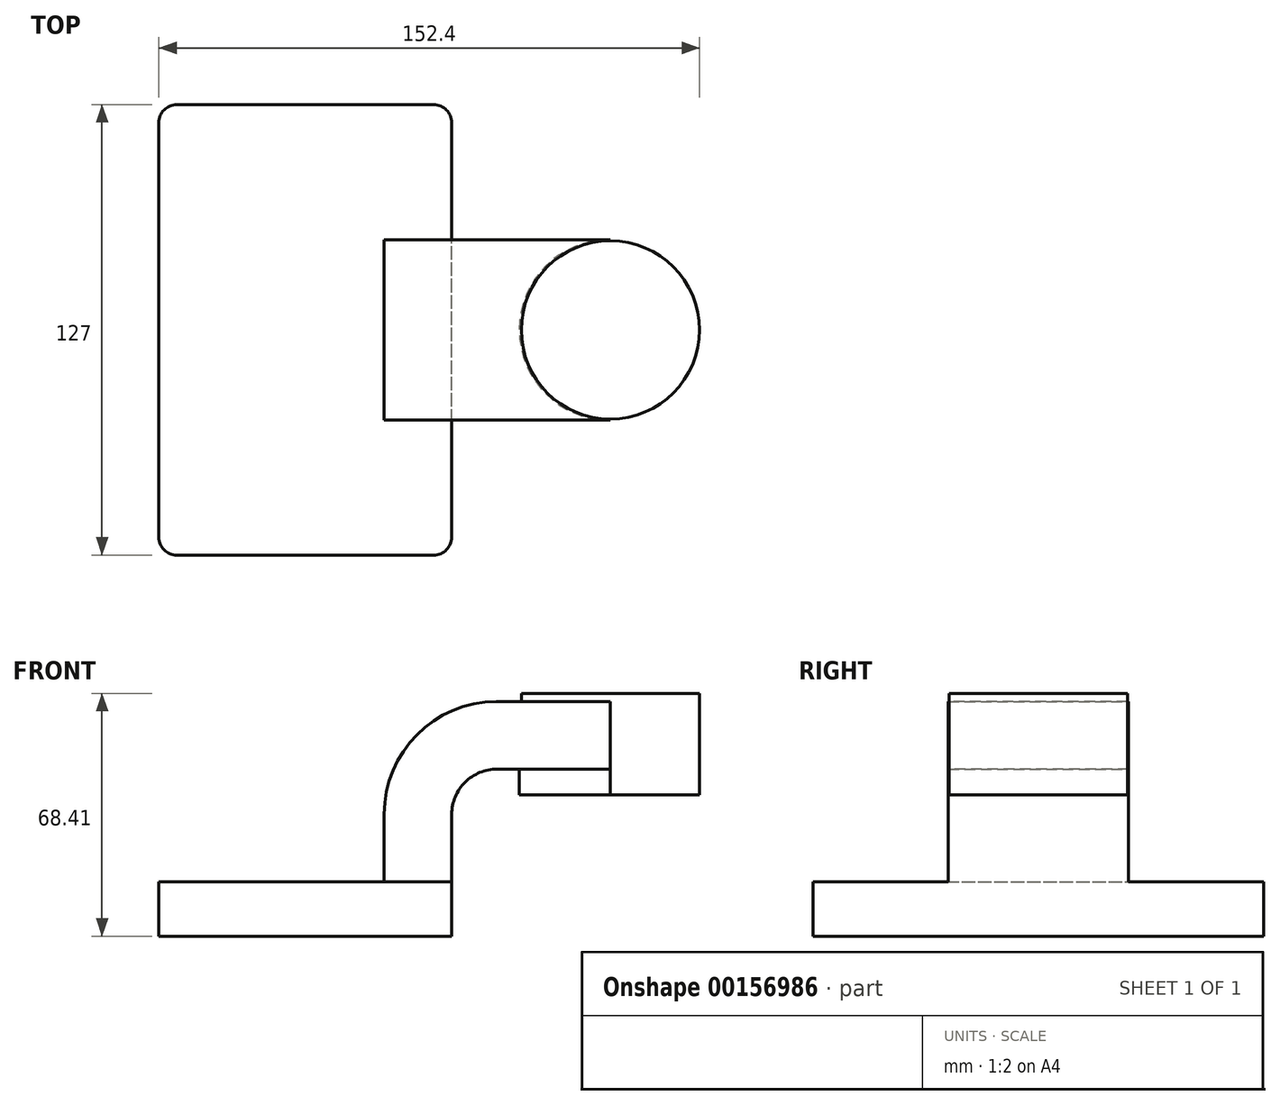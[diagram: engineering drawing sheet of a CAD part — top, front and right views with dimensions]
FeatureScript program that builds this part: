
annotation { "Feature Type Name" : "Feature", "Feature Type Description" : "" }
export const myFeature = defineFeature(function(context is Context, id is Id, definition is map)
    precondition{}
    {
        {
            var Q0;
            Q0=qCreatedBy(makeId("Front.planeOp"),FACE);
            var sketch = newSketch(context, id + "F0", { "sketchPlane" : qUnion([Q0])});
            skLineSegment(sketch, "E0.bottom", {"start": v(-41.28, -7.66) * mm, "end": v(41.28, -7.66) * mm});
            skLineSegment(sketch, "E0.top", {"start": v(-41.28, 7.66) * mm, "end": v(41.28, 7.66) * mm});
            skLineSegment(sketch, "E0.left", {"start": v(-41.28, -7.66) * mm, "end": v(-41.28, 7.66) * mm});
            skLineSegment(sketch, "E0.right", {"start": v(41.28, -7.66) * mm, "end": v(41.28, 7.66) * mm});
            skPoint(sketch, "E0.middle", {"position": v(0, 0) * mm});
            skLineSegment(sketch, "E1.bottom", {"start": v(111.13, 32.17) * mm, "end": v(60.33, 32.17) * mm});
            skLineSegment(sketch, "E1.top", {"start": v(111.13, 60.75) * mm, "end": v(60.33, 60.75) * mm});
            skLineSegment(sketch, "E1.left", {"start": v(111.13, 32.17) * mm, "end": v(111.13, 60.75) * mm});
            skLineSegment(sketch, "E1.right", {"start": v(60.33, 32.17) * mm, "end": v(60.33, 60.75) * mm});
            skPoint(sketch, "E1.middle", {"position": v(85.73, 46.46) * mm});
            skLineSegment(sketch, "E2", {"start": v(41.28, 7.66) * mm, "end": v(41.28, 26.71) * mm});
            skArc(sketch, "E3", {"start": v(41.28, 26.71) * mm, "mid": v(45.03, 35.72) * mm, "end": v(54.06, 39.41) * mm});
            skLineSegment(sketch, "E4", {"start": v(54.06, 39.41) * mm, "end": v(85.81, 39.41) * mm});
            skLineSegment(sketch, "E5.0", {"start": v(53.83, 58.46) * mm, "end": v(86, 58.46) * mm});
            skArc(sketch, "E5.1", {"start": v(22.23, 26.71) * mm, "mid": v(31.47, 49.11) * mm, "end": v(53.83, 58.46) * mm});
            skLineSegment(sketch, "E5.2", {"start": v(22.23, 7.66) * mm, "end": v(22.23, 26.71) * mm});
            skLineSegment(sketch, "E6", {"start": v(86, 60.75) * mm, "end": v(86, 32.17) * mm});
            skFitSpline(sketch, "E7", {"points": [v(-41.28, 7.66) * mm, v(53.83, 58.46) * mm], "startDerivative": vector(1.3, 78.53) * mm, "endDerivative": vector(79.63, -2.68) * mm});
            skSolve(sketch);
        }
        {
            var Q0;
            Q0=makeQuery(id+"F0.imprint","IMPRINT",FACE,{"disambiguationData":[TD([[makeQuery(id+"F0.imprint","IMPRINT",EDGE,{"derivedFrom":sQuery(id+"F0.wireOp",EDGE,"E0.bottom")}),1.0]])]});
            extrude(context, id + "F1", {"entities" : qUnion([Q0]), "endBound" : BoundingType.SYMMETRIC, "depth" : 127 * mm});
        }
        {
            var Q0;
            {var subQ2=sQuery(id+"F0.wireOp",EDGE,"E2");Q0=makeQuery(id+"F0.imprint","IMPRINT",FACE,{"disambiguationData":[TD([[makeQuery(id+"F0.imprint","IMPRINT",EDGE,{"derivedFrom":subQ2}),1.0]])]});}
            extrude(context, id + "F2", {"entities" : qUnion([Q0]), "operationType" : NewBodyOperationType.ADD, "endBound" : BoundingType.SYMMETRIC, "depth" : 50.8 * mm});
        }
        {
            var Q0;
            Q0=makeQuery(id+"F0.imprint","IMPRINT",FACE,{"disambiguationData":[TD([[makeQuery(id+"F0.imprint","IMPRINT",EDGE,{"derivedFrom":sQuery(id+"F0.wireOp",EDGE,"E5.1")}),1.0]])]});
            extrude(context, id + "F3", {"entities" : qUnion([Q0]), "operationType" : NewBodyOperationType.ADD, "endBound" : BoundingType.SYMMETRIC, "depth" : 16.5 * mm});
        }
        {
            var Q0;
            {var subQ3=sQuery(id+"F0.wireOp",EDGE,"E1.right");var subQ5=sQuery(id+"F0.wireOp",EDGE,"E1.bottom");var subQ6=makeQuery(id+"F0.imprint","INTERSECT",VERTEX,{"derivedFrom":[subQ5,subQ3]});Q0=makeQuery(id+"F0.imprint","IMPRINT",FACE,{"disambiguationData":[TD([[makeQuery(id+"F0.imprint","IMPRINT",EDGE,{"disambiguationData":[TD([[subQ6,1.0]])],"derivedFrom":subQ5}),-1.0]])]});}
            extrude(context, id + "F4", {"entities" : qUnion([Q0]), "operationType" : NewBodyOperationType.ADD, "endBound" : BoundingType.SYMMETRIC, "depth" : 50.8 * mm});
        }
        {
            var Q0;
            {var subQ0=sQuery(id+"F0.wireOp",EDGE,"E1.left");Q0=makeQuery(id+"F0.imprint","IMPRINT",FACE,{"disambiguationData":[TD([[makeQuery(id+"F0.imprint","IMPRINT",EDGE,{"derivedFrom":subQ0}),1.0]])]});}
            var Q1;
            Q1=sQuery(id+"F0.wireOp",EDGE,"E6");
            revolve(context, id + "F5", {"operationType" : NewBodyOperationType.ADD, "entities" : qUnion([Q0]), "axis" : qUnion([Q1]), "revolveType" : RevolveType.FULL});
        }
        {
            var Q0;
            Q0=makeQuery(id+"F4.opExtrude","CAP_EDGE",EDGE,{"disambiguationData":[OSD([sQuery(id+"F0.wireOp",EDGE,"E1.right")])],"isStart":false});
            var Q1;
            Q1=makeQuery(id+"F4.opExtrude","CAP_EDGE",EDGE,{"disambiguationData":[OSD([sQuery(id+"F0.wireOp",EDGE,"E1.right")])],"isStart":true});
            fillet(context, id + "F6", {"entities" : qUnion([Q0, Q1]), "radius" : 25.4 * mm, "tangentPropagation" : true, "allowEdgeOverflow" : false});
        }
        {
            var Q0;
            Q0=makeQuery(id+"F1.opExtrude","CAP_EDGE",EDGE,{"disambiguationData":[OSD([sQuery(id+"F0.wireOp",EDGE,"E0.left")])],"isStart":true});
            var Q1;
            Q1=makeQuery(id+"F1.opExtrude","CAP_EDGE",EDGE,{"disambiguationData":[OSD([sQuery(id+"F0.wireOp",EDGE,"E0.left")])],"isStart":false});
            var Q2;
            Q2=makeQuery(id+"F1.opExtrude","CAP_EDGE",EDGE,{"disambiguationData":[OSD([sQuery(id+"F0.wireOp",EDGE,"E0.right")])],"isStart":false});
            var Q3;
            Q3=makeQuery(id+"F1.opExtrude","CAP_EDGE",EDGE,{"disambiguationData":[OSD([sQuery(id+"F0.wireOp",EDGE,"E0.right")])],"isStart":true});
            fillet(context, id + "F7", {"entities" : qUnion([Q0, Q1, Q2, Q3]), "radius" : 5.08 * mm, "tangentPropagation" : true, "allowEdgeOverflow" : false});
        }
    });
